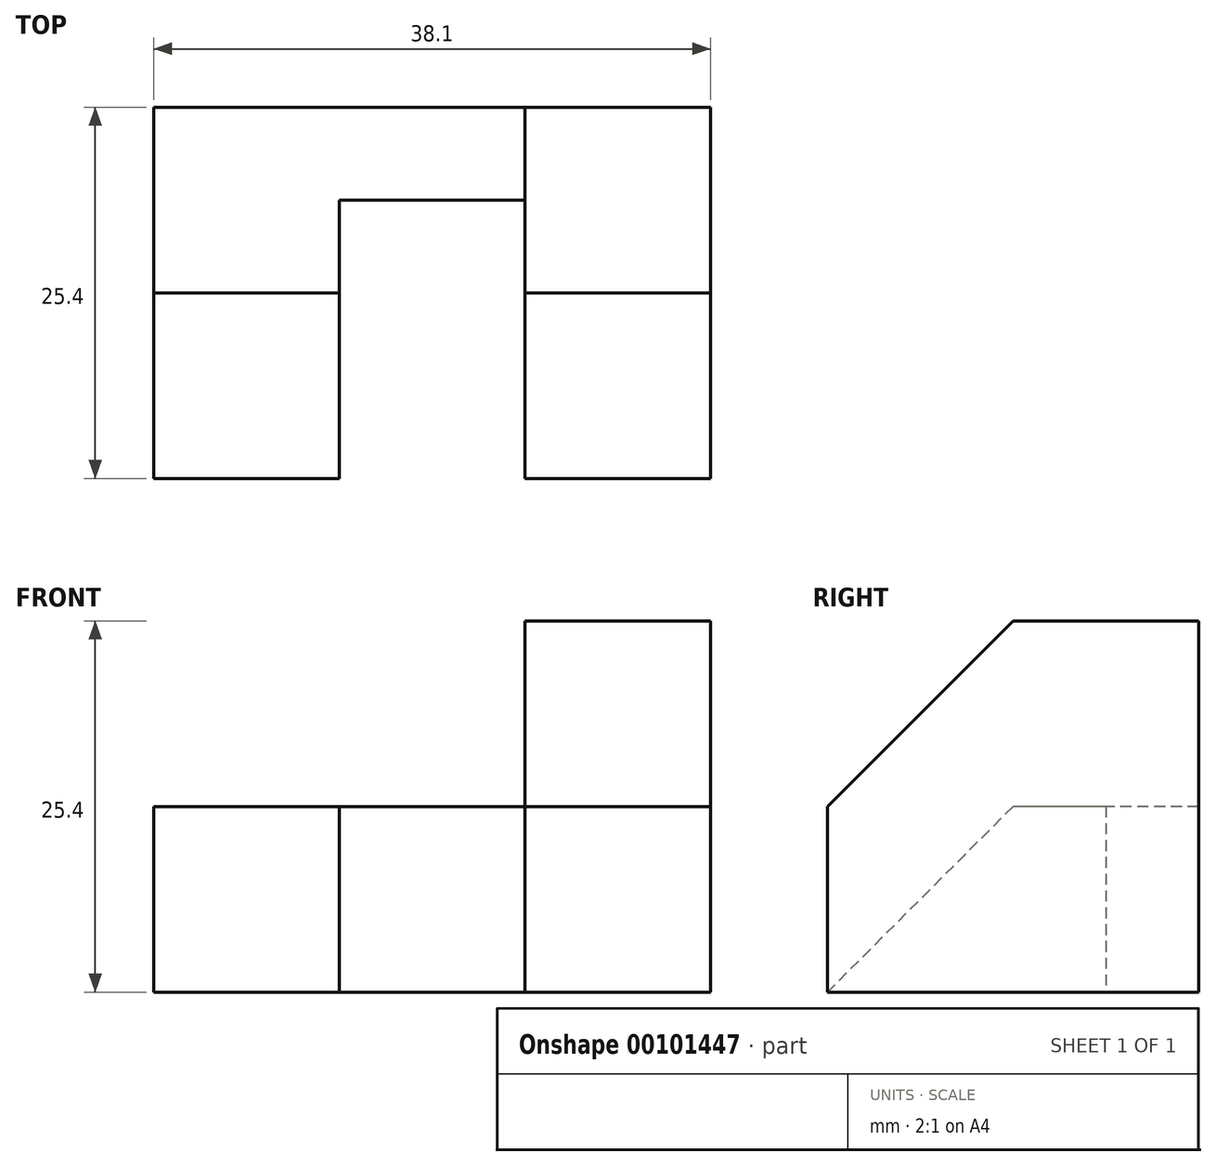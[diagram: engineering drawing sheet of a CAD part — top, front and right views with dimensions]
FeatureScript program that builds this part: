
annotation { "Feature Type Name" : "Feature", "Feature Type Description" : "" }
export const myFeature = defineFeature(function(context is Context, id is Id, definition is map)
    precondition{}
    {
        {
            var Q0;
            Q0=qCreatedBy(makeId("Right.planeOp"),FACE);
            var sketch = newSketch(context, id + "F0", { "sketchPlane" : qUnion([Q0])});
            skLineSegment(sketch, "E0", {"start": v(0, 0) * mm, "end": v(25.4, 0) * mm});
            skLineSegment(sketch, "E1", {"start": v(25.4, 0) * mm, "end": v(25.4, 12.7) * mm});
            skLineSegment(sketch, "E2", {"start": v(25.4, 12.7) * mm, "end": v(12.7, 12.7) * mm});
            skLineSegment(sketch, "E3", {"start": v(12.7, 12.7) * mm, "end": v(0, 0) * mm});
            skSolve(sketch);
        }
        {
            var Q0;
            Q0 = qSketchRegion(id + "F0", true);
            extrude(context, id + "F1", {"entities" : qUnion([Q0]), "depth" : 12.7 * mm});
        }
        {
            var Q0;
            Q0=makeQuery(id+"F1.opExtrude","CAP_FACE",FACE,{"disambiguationData":[OSD([sQuery(id+"F0.wireOp",EDGE,"E0"),sQuery(id+"F0.wireOp",EDGE,"E1"),sQuery(id+"F0.wireOp",EDGE,"E2"),sQuery(id+"F0.wireOp",EDGE,"E3")])],"isStart":false});
            var sketch = newSketch(context, id + "F2", { "sketchPlane" : qUnion([Q0])});
            skLineSegment(sketch, "E4", {"start": v(25.4, 0) * mm, "end": v(25.4, 12.7) * mm});
            skLineSegment(sketch, "E5", {"start": v(25.4, 12.7) * mm, "end": v(19.05, 12.7) * mm});
            skLineSegment(sketch, "E6", {"start": v(19.05, 12.7) * mm, "end": v(19.05, 0) * mm});
            skLineSegment(sketch, "E7", {"start": v(19.05, 0) * mm, "end": v(25.4, 0) * mm});
            skSolve(sketch);
        }
        {
            var Q0;
            Q0 = qSketchRegion(id + "F2", true);
            extrude(context, id + "F3", {"entities" : qUnion([Q0]), "operationType" : NewBodyOperationType.ADD, "depth" : 12.7 * mm});
        }
        {
            var Q0;
            Q0=makeQuery(id+"F3.opExtrude","CAP_FACE",FACE,{"disambiguationData":[OSD([sQuery(id+"F2.wireOp",EDGE,"E4"),sQuery(id+"F2.wireOp",EDGE,"E5"),sQuery(id+"F2.wireOp",EDGE,"E6"),sQuery(id+"F2.wireOp",EDGE,"E7")])],"isStart":false});
            var sketch = newSketch(context, id + "F4", { "sketchPlane" : qUnion([Q0])});
            skLineSegment(sketch, "E8", {"start": v(25.4, 0) * mm, "end": v(25.4, 25.4) * mm});
            skLineSegment(sketch, "E9", {"start": v(25.4, 25.4) * mm, "end": v(12.7, 25.4) * mm});
            skLineSegment(sketch, "E10", {"start": v(12.7, 25.4) * mm, "end": v(0, 12.7) * mm});
            skLineSegment(sketch, "E11", {"start": v(0, 12.7) * mm, "end": v(0, 0) * mm});
            skLineSegment(sketch, "E12", {"start": v(0, 0) * mm, "end": v(25.4, 0) * mm});
            skSolve(sketch);
        }
        {
            var Q0;
            Q0 = qSketchRegion(id + "F4", true);
            extrude(context, id + "F5", {"entities" : qUnion([Q0]), "operationType" : NewBodyOperationType.ADD, "depth" : 12.7 * mm});
        }
    });
